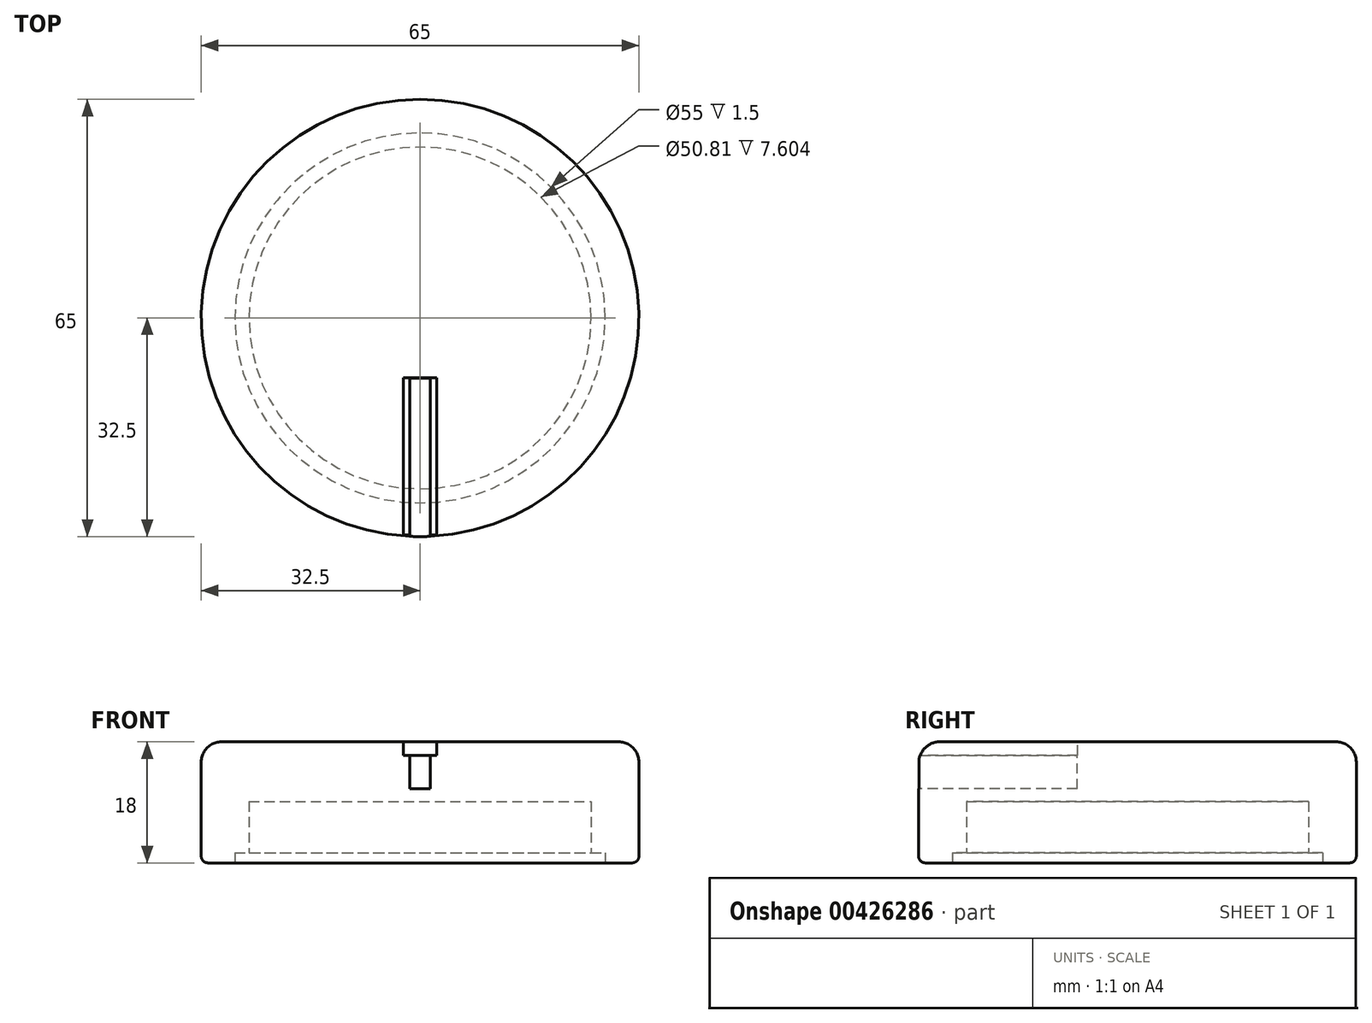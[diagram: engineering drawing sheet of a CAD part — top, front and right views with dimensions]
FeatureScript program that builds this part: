
annotation { "Feature Type Name" : "Feature", "Feature Type Description" : "" }
export const myFeature = defineFeature(function(context is Context, id is Id, definition is map)
    precondition{}
    {
        {
            var Q0;
            Q0=qCreatedBy(makeId("Top.planeOp"),FACE);
            var sketch = newSketch(context, id + "F0", { "sketchPlane" : qUnion([Q0])});
            skCircle(sketch, "E0", {"center": v(0, 0) * mm, "radius": 32.5 * mm});
            skSolve(sketch);
        }
        {
            var Q0;
            Q0=makeQuery(id+"F0.imprint","IMPRINT",FACE,{"disambiguationData":[TD([[makeQuery(id+"F0.imprint","IMPRINT",EDGE,{"derivedFrom":sQuery(id+"F0.wireOp",EDGE,"E0")}),1.0]])]});
            extrude(context, id + "F1", {"entities" : qUnion([Q0]), "depth" : 18 * mm});
        }
        {
            var Q0;
            Q0=makeQuery(id+"F1.opExtrude","CAP_EDGE",EDGE,{"disambiguationData":[OSD([sQuery(id+"F0.wireOp",EDGE,"E0")])],"isStart":false});
            fillet(context, id + "F2", {"entities" : qUnion([Q0]), "radius" : 3 * mm, "tangentPropagation" : true, "allowEdgeOverflow" : false});
        }
        {
            var Q0;
            Q0=makeQuery(id+"F1.opExtrude","CAP_EDGE",EDGE,{"disambiguationData":[OSD([sQuery(id+"F0.wireOp",EDGE,"E0")])],"isStart":true});
            fillet(context, id + "F3", {"entities" : qUnion([Q0]), "radius" : 1 * mm, "tangentPropagation" : true, "allowEdgeOverflow" : false});
        }
        {
            var Q0;
            Q0=makeQuery(id+"F1.opExtrude","CAP_FACE",FACE,{"disambiguationData":[OSD([sQuery(id+"F0.wireOp",EDGE,"E0")])],"isStart":true});
            var sketch = newSketch(context, id + "F4", { "sketchPlane" : qUnion([Q0])});
            skCircle(sketch, "E1", {"center": v(0, 0) * mm, "radius": 25.4 * mm});
            skSolve(sketch);
        }
        {
            var Q0;
            Q0=makeQuery(id+"F4.imprint","IMPRINT",FACE,{"disambiguationData":[TD([[makeQuery(id+"F4.imprint","IMPRINT",EDGE,{"derivedFrom":sQuery(id+"F4.wireOp",EDGE,"E1")}),1.0]])]});
            extrude(context, id + "F5", {"entities" : qUnion([Q0]), "operationType" : NewBodyOperationType.REMOVE, "oppositeDirection" : true, "depth" : 9.1 * mm});
        }
        {
            var Q0;
            Q0=makeQuery(id+"F1.opExtrude","CAP_FACE",FACE,{"disambiguationData":[OSD([sQuery(id+"F0.wireOp",EDGE,"E0")])],"isStart":true});
            var sketch = newSketch(context, id + "F6", { "sketchPlane" : qUnion([Q0])});
            skCircle(sketch, "E2", {"center": v(0, 0) * mm, "radius": 27.5 * mm});
            skSolve(sketch);
        }
        {
            var Q0;
            Q0=makeQuery(id+"F6.imprint","IMPRINT",FACE,{"disambiguationData":[TD([[makeQuery(id+"F6.imprint","IMPRINT",EDGE,{"derivedFrom":sQuery(id+"F6.wireOp",EDGE,"E2")}),1.0]])]});
            extrude(context, id + "F7", {"entities" : qUnion([Q0]), "operationType" : NewBodyOperationType.REMOVE, "oppositeDirection" : true, "depth" : 1.5 * mm});
        }
        {
            var Q0;
            Q0=makeQuery(id+"F1.opExtrude","CAP_FACE",FACE,{"disambiguationData":[OSD([sQuery(id+"F0.wireOp",EDGE,"E0")])],"isStart":false});
            var sketch = newSketch(context, id + "F8", { "sketchPlane" : qUnion([Q0])});
            skLineSegment(sketch, "E3", {"start": v(0, -8.96) * mm, "end": v(1.55, -8.96) * mm});
            skLineSegment(sketch, "E4", {"start": v(1.55, -8.96) * mm, "end": v(1.55, -32.46) * mm});
            skLineSegment(sketch, "E5.MirrorCS", {"start": v(0, -8.96) * mm, "end": v(-1.55, -8.96) * mm});
            skLineSegment(sketch, "E6.MirrorCS", {"start": v(-1.55, -8.96) * mm, "end": v(-1.55, -32.46) * mm});
            skArc(sketch, "E7.0", {"start": v(-1.55, -32.46) * mm, "mid": v(0, -32.5) * mm, "end": v(1.55, -32.46) * mm});
            skSolve(sketch);
        }
        {
            var Q0;
            {var subQ6=sQuery(id+"F8.wireOp",EDGE,"E3");Q0=makeQuery(id+"F8.imprint","IMPRINT",FACE,{"disambiguationData":[TD([[makeQuery(id+"F8.imprint","IMPRINT",EDGE,{"derivedFrom":subQ6}),-1.0]])]});}
            var Q1;
            {var subQ0=sQuery(id+"F8.wireOp",EDGE,"E7.0");var subQ1=sQuery(id+"F8.wireOp",EDGE,"E4");var subQ2=makeQuery(id+"F8.imprint","INTERSECT",VERTEX,{"derivedFrom":[subQ1,subQ0]});Q1=makeQuery(id+"F8.imprint","IMPRINT",FACE,{"disambiguationData":[TD([[makeQuery(id+"F8.imprint","IMPRINT",EDGE,{"disambiguationData":[TD([[subQ2,1.0]])],"derivedFrom":subQ0}),1.0]])]});}
            extrude(context, id + "F9", {"entities" : qUnion([Q0, Q1]), "operationType" : NewBodyOperationType.REMOVE, "oppositeDirection" : true, "depth" : 7 * mm});
        }
        {
            var Q0;
            Q0=makeQuery(id+"F1.opExtrude","CAP_FACE",FACE,{"disambiguationData":[OSD([sQuery(id+"F0.wireOp",EDGE,"E0")])],"isStart":false});
            var sketch = newSketch(context, id + "F10", { "sketchPlane" : qUnion([Q0])});
            skArc(sketch, "E8.0", {"start": v(-1.55, -32.46) * mm, "mid": v(-2.03, -32.44) * mm, "end": v(-2.5, -32.4) * mm});
            skLineSegment(sketch, "E9", {"start": v(2.5, -8.9) * mm, "end": v(2.5, -32.4) * mm});
            skLineSegment(sketch, "E10.MirrorCS", {"start": v(-2.5, -8.9) * mm, "end": v(-2.5, -32.4) * mm});
            skArc(sketch, "E11.trimOffspring", {"start": v(2.5, -32.4) * mm, "mid": v(2.03, -32.44) * mm, "end": v(1.55, -32.46) * mm});
            skArc(sketch, "E12.0", {"start": v(-1.55, -32.46) * mm, "mid": v(0, -32.5) * mm, "end": v(1.55, -32.46) * mm});
            skLineSegment(sketch, "E13", {"start": v(-2.5, -8.9) * mm, "end": v(2.5, -8.9) * mm});
            skSolve(sketch);
        }
        {
            var Q0;
            Q0 = qSketchRegion(id + "F10", true);
            extrude(context, id + "F11", {"entities" : qUnion([Q0]), "operationType" : NewBodyOperationType.REMOVE, "oppositeDirection" : true, "depth" : 2 * mm});
        }
        {
            var Q0;
            Q0=makeQuery(id+"F1.opExtrude","CAP_FACE",FACE,{"disambiguationData":[OSD([sQuery(id+"F0.wireOp",EDGE,"E0")])],"isStart":true});
            var sketch = newSketch(context, id + "F12", { "sketchPlane" : qUnion([Q0])});
            skCircle(sketch, "E14", {"center": v(0, 0) * mm, "radius": 32.25 * mm});
            skSolve(sketch);
        }
        {
            var Q0;
            Q0 = qSketchRegion(id + "F12", true);
            var Q1;
            Q1 = qConstructionFilter(qBodyType(qCreatedBy(id + "F12" ,EDGE), BodyType.WIRE), ConstructionObject.NO);
            extrude(context, id + "F13", {"entities" : qUnion([Q0]), "bodyType" : ToolBodyType.SURFACE, "operationType" : NewBodyOperationType.INTERSECT, "surfaceEntities" : qUnion([Q1]), "oppositeDirection" : true, "depth" : 15.8 * mm});
        }
        {
            var Q0;
            {var subQ0=sQuery(id+"F0.wireOp",EDGE,"E0");Q0=makeQuery(id+"F2.opFillet","BLEND_EDGE",EDGE,{"blendedFrom":[makeQuery(id+"F1.opExtrude","CAP_EDGE",EDGE,{"disambiguationData":[OSD([subQ0])],"isStart":false}),makeQuery(id+"F1.opExtrude","SWEPT_FACE",FACE,{"disambiguationData":[OSD([subQ0])]})],"blendedInto":[makeQuery(id+"F1.opExtrude","SWEPT_FACE",FACE,{"disambiguationData":[OSD([subQ0])]})]});}
            cPlane(context, id + "F14", {"entities" : qUnion([Q0]), "cplaneType" : CPlaneType.LINE_ANGLE, "offset" : 39 * mm, "angle" : 180 * degree, "oppositeDirection" : true, "width" : 150 * mm, "height" : 150 * mm});
        }
    });
